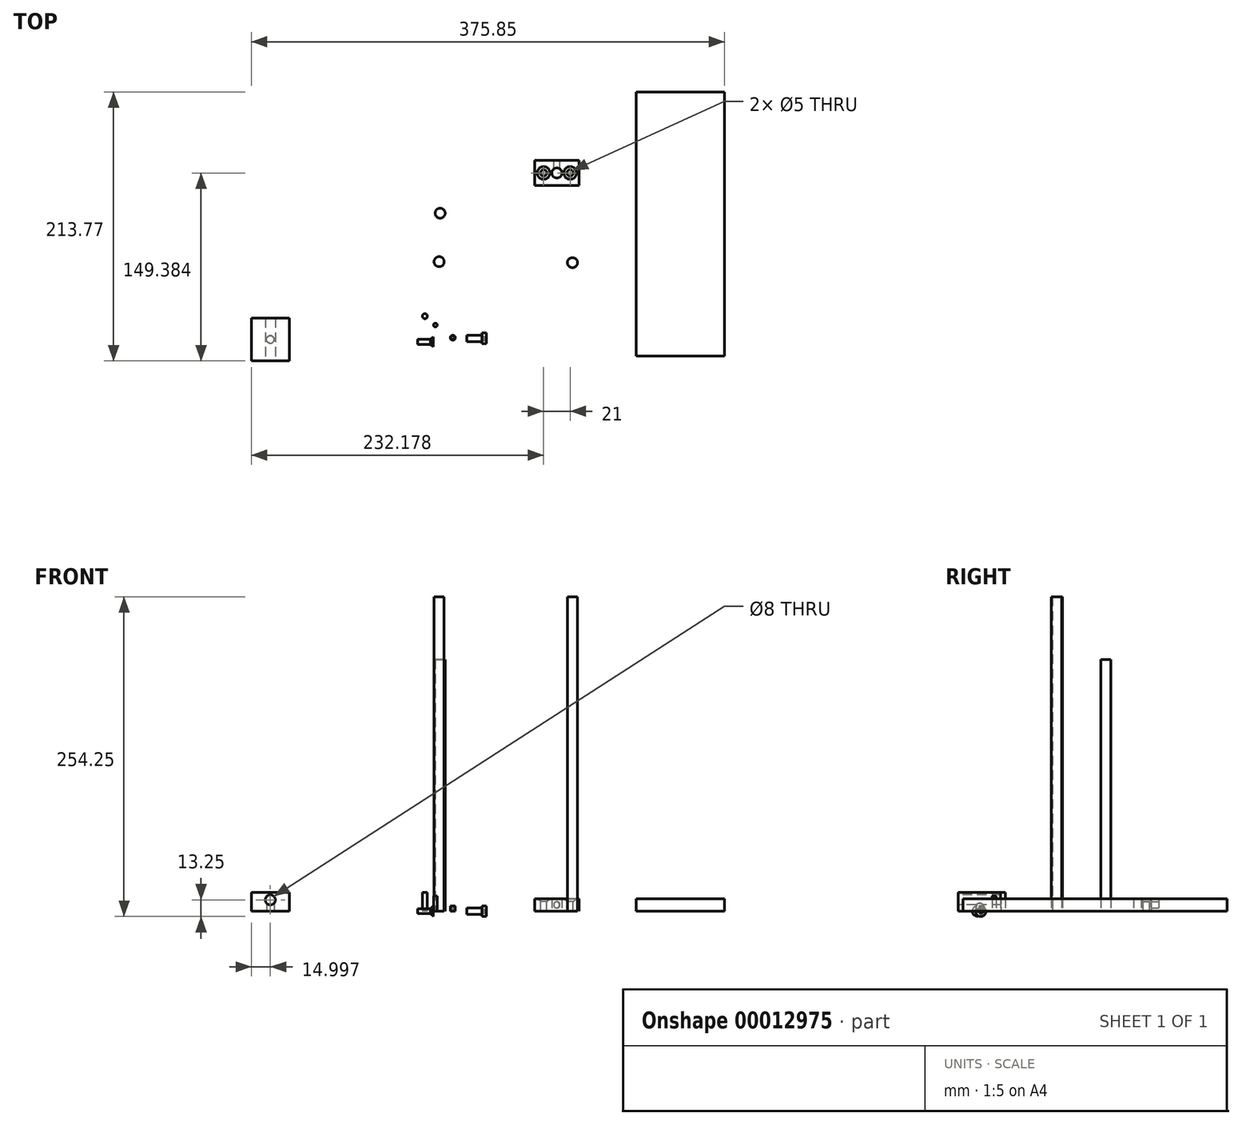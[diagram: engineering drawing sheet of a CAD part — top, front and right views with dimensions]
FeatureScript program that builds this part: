
annotation { "Feature Type Name" : "Feature", "Feature Type Description" : "" }
export const myFeature = defineFeature(function(context is Context, id is Id, definition is map)
    precondition{}
    {
        {
            var Q0;
            Q0=qCreatedBy(makeId("Top.planeOp"),FACE);
            var sketch = newSketch(context, id + "F0", { "sketchPlane" : qUnion([Q0])});
            skCircle(sketch, "E0", {"center": v(-56.15, 28.81) * mm, "radius": 4 * mm});
            skCircle(sketch, "E1", {"center": v(-56.98, -9.72) * mm, "radius": 4 * mm});
            skSolve(sketch);
        }
        {
            var Q0;
            Q0=makeQuery(id+"F0.imprint","IMPRINT",FACE,{"disambiguationData":[TD([[makeQuery(id+"F0.imprint","IMPRINT",EDGE,{"derivedFrom":sQuery(id+"F0.wireOp",EDGE,"E0")}),1.0]])]});
            extrude(context, id + "F1", {"entities" : qUnion([Q0]), "depth" : 200 * mm});
        }
        {
            var Q0;
            Q0=makeQuery(id+"F0.imprint","IMPRINT",FACE,{"disambiguationData":[TD([[makeQuery(id+"F0.imprint","IMPRINT",EDGE,{"derivedFrom":sQuery(id+"F0.wireOp",EDGE,"E1")}),1.0]])]});
            extrude(context, id + "F2", {"entities" : qUnion([Q0]), "depth" : 250 * mm});
        }
        {
            var Q0;
            Q0=qCreatedBy(makeId("Top.planeOp"),FACE);
            var sketch = newSketch(context, id + "F3", { "sketchPlane" : qUnion([Q0])});
            skCircle(sketch, "E2", {"center": v(48.96, -10.46) * mm, "radius": 4 * mm});
            skSolve(sketch);
        }
        {
            var Q0;
            Q0=makeQuery(id+"F3.imprint","IMPRINT",FACE,{"disambiguationData":[TD([[makeQuery(id+"F3.imprint","IMPRINT",EDGE,{"derivedFrom":sQuery(id+"F3.wireOp",EDGE,"E2")}),1.0]])]});
            extrude(context, id + "F4", {"entities" : qUnion([Q0]), "depth" : 250 * mm});
        }
        {
            var Q0;
            Q0=qCreatedBy(makeId("Top.planeOp"),FACE);
            var sketch = newSketch(context, id + "F5", { "sketchPlane" : qUnion([Q0])});
            skLineSegment(sketch, "E3.bottom", {"start": v(-77.13, -28.76) * mm, "end": v(-37.13, -28.76) * mm});
            skLineSegment(sketch, "E3.top", {"start": v(-77.13, -68.76) * mm, "end": v(-37.13, -68.76) * mm});
            skLineSegment(sketch, "E3.left", {"start": v(-77.13, -28.76) * mm, "end": v(-77.13, -68.76) * mm});
            skLineSegment(sketch, "E3.right", {"start": v(-37.13, -28.76) * mm, "end": v(-37.13, -68.76) * mm});
            skCircle(sketch, "E4", {"center": v(-57.13, -48.76) * mm, "radius": 4 * mm});
            skPoint(sketch, "E4.centerSnap0", {"position": v(-37.13, -48.76) * mm});
            skSolve(sketch);
        }
        {
            var Q0;
            Q0 = qSketchRegion(id + "F5", true);
            extrude(context, id + "F6", {"entities" : qUnion([Q0]), "depth" : 25 * mm});
        }
        {
            var Q0;
            Q0=qCreatedBy(makeId("Top.planeOp"),FACE);
            var sketch = newSketch(context, id + "F7", { "sketchPlane" : qUnion([Q0])});
            skLineSegment(sketch, "E5.bottom", {"start": v(-206.1, -54.52) * mm, "end": v(-176.1, -54.52) * mm});
            skLineSegment(sketch, "E5.top", {"start": v(-206.1, -88.52) * mm, "end": v(-176.1, -88.52) * mm});
            skLineSegment(sketch, "E5.left", {"start": v(-206.1, -54.52) * mm, "end": v(-206.1, -88.52) * mm});
            skLineSegment(sketch, "E5.right", {"start": v(-176.1, -54.52) * mm, "end": v(-176.1, -88.52) * mm});
            skPoint(sketch, "E6.centerSnap0", {"position": v(-191.1, -54.52) * mm});
            skSolve(sketch);
        }
        {
            var Q0;
            Q0 = qSketchRegion(id + "F7", true);
            extrude(context, id + "F8", {"entities" : qUnion([Q0]), "depth" : 15 * mm});
        }
        {
            var Q0;
            Q0=qCreatedBy(makeId("Top.planeOp"),FACE);
            var sketch = newSketch(context, id + "F9", { "sketchPlane" : qUnion([Q0])});
            skLineSegment(sketch, "E7.bottom", {"start": v(99.75, 125.25) * mm, "end": v(169.75, 125.25) * mm});
            skLineSegment(sketch, "E7.top", {"start": v(99.75, -84.75) * mm, "end": v(169.75, -84.75) * mm});
            skLineSegment(sketch, "E7.left", {"start": v(99.75, 125.25) * mm, "end": v(99.75, -84.75) * mm});
            skLineSegment(sketch, "E7.right", {"start": v(169.75, 125.25) * mm, "end": v(169.75, -84.75) * mm});
            skSolve(sketch);
        }
        {
            var Q0;
            Q0 = qSketchRegion(id + "F9", true);
            extrude(context, id + "F10", {"entities" : qUnion([Q0]), "depth" : 10 * mm});
        }
        {
            var Q0;
            Q0=makeQuery(id+"F6.opExtrude","SWEPT_BODY",BODY,{"disambiguationData":[OSD([sQuery(id+"F5.wireOp",EDGE,"E3.bottom"),sQuery(id+"F5.wireOp",EDGE,"E3.top"),sQuery(id+"F5.wireOp",EDGE,"E3.left"),sQuery(id+"F5.wireOp",EDGE,"E3.right"),sQuery(id+"F5.wireOp",EDGE,"E4")])]});
            deleteBodies(context, id + "F11", {"entities" : qUnion([Q0])});
        }
        {
            var Q0;
            Q0=makeQuery(id+"F8.opExtrude","SWEPT_FACE",FACE,{"disambiguationData":[OSD([sQuery(id+"F7.wireOp",EDGE,"E5.top")])]});
            var sketch = newSketch(context, id + "F12", { "sketchPlane" : qUnion([Q0])});
            skCircle(sketch, "E8", {"center": v(-191.1, 9) * mm, "radius": 4 * mm});
            skSolve(sketch);
        }
        {
            var Q0;
            Q0 = qSketchRegion(id + "F12", true);
            extrude(context, id + "F13", {"entities" : qUnion([Q0]), "operationType" : NewBodyOperationType.REMOVE, "endBound" : BoundingType.THROUGH_ALL, "oppositeDirection" : true, "depth" : 25 * mm});
        }
        {
            var Q0;
            Q0=makeQuery(id+"F8.opExtrude","CAP_FACE",FACE,{"disambiguationData":[OSD([sQuery(id+"F7.wireOp",EDGE,"E5.bottom"),sQuery(id+"F7.wireOp",EDGE,"E5.top"),sQuery(id+"F7.wireOp",EDGE,"E5.left"),sQuery(id+"F7.wireOp",EDGE,"E5.right")])],"isStart":true});
            var sketch = newSketch(context, id + "F14", { "sketchPlane" : qUnion([Q0])});
            skLineSegment(sketch, "E9", {"start": v(-191.1, 88.52) * mm, "end": v(-191.1, 54.52) * mm, "construction": true});
            skLineSegment(sketch, "E10", {"start": v(-206.1, 71.52) * mm, "end": v(-176.1, 71.52) * mm, "construction": true});
            skCircle(sketch, "E11", {"center": v(-191.1, 71.52) * mm, "radius": 3 * mm});
            skSolve(sketch);
        }
        {
            var Q0;
            Q0 = qSketchRegion(id + "F14", true);
            extrude(context, id + "F15", {"entities" : qUnion([Q0]), "operationType" : NewBodyOperationType.REMOVE, "oppositeDirection" : true, "depth" : 7 * mm});
        }
        {
            var Q0;
            Q0=qCreatedBy(makeId("Top.planeOp"),FACE);
            var sketch = newSketch(context, id + "F16", { "sketchPlane" : qUnion([Q0])});
            skCircle(sketch, "E12", {"center": v(-60, -60.01) * mm, "radius": 1.5 * mm});
            skSolve(sketch);
        }
        {
            var Q0;
            Q0 = qSketchRegion(id + "F16", true);
            extrude(context, id + "F17", {"entities" : qUnion([Q0]), "depth" : 12 * mm});
        }
        {
            var Q0;
            Q0=qCreatedBy(makeId("Top.planeOp"),FACE);
            var sketch = newSketch(context, id + "F18", { "sketchPlane" : qUnion([Q0])});
            skLineSegment(sketch, "E13", {"start": v(-35.05, -70.66) * mm, "end": v(-35.05, -68.16) * mm});
            skLineSegment(sketch, "E14", {"start": v(-35.05, -68.16) * mm, "end": v(-23.05, -68.16) * mm});
            skLineSegment(sketch, "E15", {"start": v(-23.05, -68.16) * mm, "end": v(-23.05, -66.4) * mm});
            skLineSegment(sketch, "E16", {"start": v(-23.05, -66.4) * mm, "end": v(-19.55, -66.4) * mm});
            skLineSegment(sketch, "E17", {"start": v(-19.55, -66.4) * mm, "end": v(-19.55, -70.66) * mm});
            skLineSegment(sketch, "E18", {"start": v(-19.55, -70.66) * mm, "end": v(-35.05, -70.66) * mm});
            skSolve(sketch);
        }
        {
            var Q0;
            Q0 = qSketchRegion(id + "F18", true);
            var Q1;
            Q1=sQuery(id+"F18.wireOp",EDGE,"E18");
            revolve(context, id + "F19", {"entities" : qUnion([Q0]), "axis" : qUnion([Q1]), "revolveType" : RevolveType.FULL});
        }
        {
            var Q0;
            Q0=makeQuery(id+"F19.opRevolve","SWEPT_FACE",FACE,{"disambiguationData":[OSD([sQuery(id+"F18.wireOp",EDGE,"E17")])]});
            var sketch = newSketch(context, id + "F20", { "sketchPlane" : qUnion([Q0])});
            skCircle(sketch, "E19.cCircle", {"center": v(-70.66, 0) * mm, "radius": 1.5 * mm, "construction": true});
            skLineSegment(sketch, "E19.0", {"start": v(-70.28, -1.7) * mm, "end": v(-71.93, -1.17) * mm});
            skLineSegment(sketch, "E19.1", {"start": v(-71.93, -1.17) * mm, "end": v(-72.3, 0.52) * mm});
            skLineSegment(sketch, "E19.2", {"start": v(-72.3, 0.52) * mm, "end": v(-71.03, 1.7) * mm});
            skLineSegment(sketch, "E19.3", {"start": v(-71.03, 1.7) * mm, "end": v(-69.38, 1.17) * mm});
            skLineSegment(sketch, "E19.4", {"start": v(-69.38, 1.17) * mm, "end": v(-69, -0.52) * mm});
            skLineSegment(sketch, "E19.5", {"start": v(-69, -0.52) * mm, "end": v(-70.28, -1.7) * mm});
            skPoint(sketch, "E19.0.midPoint", {"position": v(-71.1, -1.43) * mm});
            skSolve(sketch);
        }
        {
            var Q0;
            Q0 = qSketchRegion(id + "F20", true);
            extrude(context, id + "F21", {"entities" : qUnion([Q0]), "operationType" : NewBodyOperationType.REMOVE, "oppositeDirection" : true, "depth" : 2 * mm});
        }
        {
            var Q0;
            Q0=qCreatedBy(makeId("Top.planeOp"),FACE);
            var sketch = newSketch(context, id + "F22", { "sketchPlane" : qUnion([Q0])});
            skCircle(sketch, "E20", {"center": v(-46.13, -70.15) * mm, "radius": 2 * mm});
            skSolve(sketch);
        }
        {
            var Q0;
            Q0 = qSketchRegion(id + "F22", true);
            extrude(context, id + "F23", {"entities" : qUnion([Q0]), "depth" : 4 * mm});
        }
        {
            var Q0;
            Q0=makeQuery(id+"F23.opExtrude","CAP_FACE",FACE,{"disambiguationData":[OSD([sQuery(id+"F22.wireOp",EDGE,"E20")])],"isStart":false});
            var sketch = newSketch(context, id + "F24", { "sketchPlane" : qUnion([Q0])});
            skCircle(sketch, "E21.cCircle", {"center": v(-46.13, -70.15) * mm, "radius": 1.5 * mm, "construction": true});
            skLineSegment(sketch, "E21.0", {"start": v(-44.4, -70.22) * mm, "end": v(-45.33, -71.69) * mm});
            skLineSegment(sketch, "E21.1", {"start": v(-45.33, -71.69) * mm, "end": v(-47.06, -71.61) * mm});
            skLineSegment(sketch, "E21.2", {"start": v(-47.06, -71.61) * mm, "end": v(-47.86, -70.08) * mm});
            skLineSegment(sketch, "E21.3", {"start": v(-47.86, -70.08) * mm, "end": v(-46.93, -68.61) * mm});
            skLineSegment(sketch, "E21.4", {"start": v(-46.93, -68.61) * mm, "end": v(-45.2, -68.69) * mm});
            skLineSegment(sketch, "E21.5", {"start": v(-45.2, -68.69) * mm, "end": v(-44.4, -70.22) * mm});
            skPoint(sketch, "E21.0.midPoint", {"position": v(-44.86, -70.95) * mm});
            skSolve(sketch);
        }
        {
            var Q0;
            Q0 = qSketchRegion(id + "F24", true);
            extrude(context, id + "F25", {"entities" : qUnion([Q0]), "operationType" : NewBodyOperationType.REMOVE, "oppositeDirection" : true, "depth" : 2 * mm});
        }
        {
            var Q0;
            Q0=qCreatedBy(makeId("Top.planeOp"),FACE);
            var sketch = newSketch(context, id + "F26", { "sketchPlane" : qUnion([Q0])});
            skLineSegment(sketch, "E22", {"start": v(-73.96, -73.4) * mm, "end": v(-73.96, -71.4) * mm});
            skLineSegment(sketch, "E23", {"start": v(-73.96, -71.4) * mm, "end": v(-63.96, -71.4) * mm});
            skLineSegment(sketch, "E24", {"start": v(-63.96, -71.4) * mm, "end": v(-61.66, -69.4) * mm});
            skLineSegment(sketch, "E25", {"start": v(-61.66, -69.4) * mm, "end": v(-61.66, -73.4) * mm});
            skLineSegment(sketch, "E26", {"start": v(-61.66, -73.4) * mm, "end": v(-73.96, -73.4) * mm});
            skSolve(sketch);
        }
        {
            var Q0;
            Q0 = qSketchRegion(id + "F26", true);
            var Q1;
            Q1=sQuery(id+"F26.wireOp",EDGE,"E26");
            revolve(context, id + "F27", {"entities" : qUnion([Q0]), "axis" : qUnion([Q1]), "revolveType" : RevolveType.FULL});
        }
        {
            var Q0;
            Q0=makeQuery(id+"F27.opRevolve","SWEPT_FACE",FACE,{"disambiguationData":[OSD([sQuery(id+"F26.wireOp",EDGE,"E25")])]});
            var sketch = newSketch(context, id + "F28", { "sketchPlane" : qUnion([Q0])});
            skCircle(sketch, "E27.cCircle", {"center": v(-73.4, 0) * mm, "radius": 1.25 * mm, "construction": true});
            skLineSegment(sketch, "E27.0", {"start": v(-73.67, -1.42) * mm, "end": v(-74.76, -0.47) * mm});
            skLineSegment(sketch, "E27.1", {"start": v(-74.76, -0.47) * mm, "end": v(-74.5, 0.94) * mm});
            skLineSegment(sketch, "E27.2", {"start": v(-74.5, 0.94) * mm, "end": v(-73.13, 1.42) * mm});
            skLineSegment(sketch, "E27.3", {"start": v(-73.13, 1.42) * mm, "end": v(-72.04, 0.47) * mm});
            skLineSegment(sketch, "E27.4", {"start": v(-72.04, 0.47) * mm, "end": v(-72.3, -0.94) * mm});
            skLineSegment(sketch, "E27.5", {"start": v(-72.3, -0.94) * mm, "end": v(-73.67, -1.42) * mm});
            skPoint(sketch, "E27.0.midPoint", {"position": v(-74.22, -0.95) * mm});
            skSolve(sketch);
        }
        {
            var Q0;
            Q0 = qSketchRegion(id + "F28", true);
            extrude(context, id + "F29", {"entities" : qUnion([Q0]), "operationType" : NewBodyOperationType.REMOVE, "oppositeDirection" : true, "depth" : 2 * mm});
        }
        {
            var Q0;
            Q0=qCreatedBy(makeId("Top.planeOp"),FACE);
            var sketch = newSketch(context, id + "F30", { "sketchPlane" : qUnion([Q0])});
            skCircle(sketch, "E28", {"center": v(-68.31, -53.04) * mm, "radius": 2 * mm});
            skSolve(sketch);
        }
        {
            var Q0;
            Q0=makeQuery(id+"F30.imprint","IMPRINT",FACE,{"disambiguationData":[TD([[makeQuery(id+"F30.imprint","IMPRINT",EDGE,{"derivedFrom":sQuery(id+"F30.wireOp",EDGE,"E28")}),1.0]])]});
            extrude(context, id + "F31", {"entities" : qUnion([Q0]), "depth" : 15 * mm});
        }
        {
            var Q0;
            Q0=qCreatedBy(makeId("Top.planeOp"),FACE);
            var sketch = newSketch(context, id + "F32", { "sketchPlane" : qUnion([Q0])});
            skLineSegment(sketch, "E29.bottom", {"start": v(19.08, 70.86) * mm, "end": v(54.08, 70.86) * mm});
            skLineSegment(sketch, "E29.top", {"start": v(19.08, 50.86) * mm, "end": v(54.08, 50.86) * mm});
            skLineSegment(sketch, "E29.left", {"start": v(19.08, 70.86) * mm, "end": v(19.08, 50.86) * mm});
            skLineSegment(sketch, "E29.right", {"start": v(54.08, 70.86) * mm, "end": v(54.08, 50.86) * mm});
            skLineSegment(sketch, "E30", {"start": v(19.08, 60.86) * mm, "end": v(54.08, 60.86) * mm, "construction": true});
            skCircle(sketch, "E31", {"center": v(36.58, 60.86) * mm, "radius": 4 * mm});
            skSolve(sketch);
        }
        {
            var Q0;
            Q0 = qSketchRegion(id + "F32", true);
            extrude(context, id + "F33", {"entities" : qUnion([Q0]), "depth" : 10 * mm});
        }
        {
            var Q0;
            Q0=makeQuery(id+"F33.opExtrude","CAP_FACE",FACE,{"disambiguationData":[OSD([sQuery(id+"F32.wireOp",EDGE,"E29.bottom"),sQuery(id+"F32.wireOp",EDGE,"E29.top"),sQuery(id+"F32.wireOp",EDGE,"E29.left"),sQuery(id+"F32.wireOp",EDGE,"E29.right"),sQuery(id+"F32.wireOp",EDGE,"E31")])],"isStart":false});
            var sketch = newSketch(context, id + "F34", { "sketchPlane" : qUnion([Q0])});
            skPoint(sketch, "E32", {"position": v(26.08, 60.86) * mm});
            skPoint(sketch, "E32.positionSnap0", {"position": v(19.08, 60.86) * mm});
            skPoint(sketch, "E33", {"position": v(47.08, 60.86) * mm});
            skPoint(sketch, "E33.positionSnap0", {"position": v(54.08, 60.86) * mm});
            skLineSegment(sketch, "E34", {"start": v(19.08, 60.86) * mm, "end": v(54.08, 60.86) * mm, "construction": true});
            skLineSegment(sketch, "E35", {"start": v(36.58, 70.86) * mm, "end": v(36.58, 50.86) * mm, "construction": true});
            skSolve(sketch);
        }
        {
            var Q0;
            Q0=sQuery(id+"F34.wireOp",VERTEX,"E32");
            var Q1;
            Q1=sQuery(id+"F34.wireOp",VERTEX,"E33");
            var Q2;
            Q2=makeQuery(id+"F33.opExtrude","SWEPT_BODY",BODY,{"disambiguationData":[OSD([sQuery(id+"F32.wireOp",EDGE,"E29.bottom"),sQuery(id+"F32.wireOp",EDGE,"E29.top"),sQuery(id+"F32.wireOp",EDGE,"E29.left"),sQuery(id+"F32.wireOp",EDGE,"E29.right"),sQuery(id+"F32.wireOp",EDGE,"E31")])]});
            hole(context, id + "F35", {"style" : HoleStyle.C_SINK, "holeDiameter" : 5 * mm, "cSinkDiameter" : 10 * mm, "endStyle" : HoleEndStyle.THROUGH, "locations" : qUnion([Q0, Q1]), "scope" : qUnion([Q2]), "cSinkAngle" : 90 * degree});
        }
        {
            var Q0;
            Q0=makeQuery(id+"F33.opExtrude","SWEPT_FACE",FACE,{"disambiguationData":[OSD([sQuery(id+"F32.wireOp",EDGE,"E29.bottom")])]});
            var sketch = newSketch(context, id + "F36", { "sketchPlane" : qUnion([Q0])});
            skLineSegment(sketch, "E36", {"start": v(-36.58, 10) * mm, "end": v(-36.58, 0) * mm, "construction": true});
            skPoint(sketch, "E37", {"position": v(-36.58, 5) * mm});
            skSolve(sketch);
        }
        {
            var Q0;
            Q0=sQuery(id+"F36.wireOp",VERTEX,"E37");
            var Q1;
            Q1=makeQuery(id+"F33.opExtrude","SWEPT_BODY",BODY,{"disambiguationData":[OSD([sQuery(id+"F32.wireOp",EDGE,"E29.bottom"),sQuery(id+"F32.wireOp",EDGE,"E29.top"),sQuery(id+"F32.wireOp",EDGE,"E29.left"),sQuery(id+"F32.wireOp",EDGE,"E29.right"),sQuery(id+"F32.wireOp",EDGE,"E31")])]});
            hole(context, id + "F37", {"style" : HoleStyle.SIMPLE, "holeDiameter" : 5 * mm, "endStyle" : HoleEndStyle.BLIND, "holeDepth" : 6 * mm, "locations" : qUnion([Q0]), "scope" : qUnion([Q1])});
        }
    });
